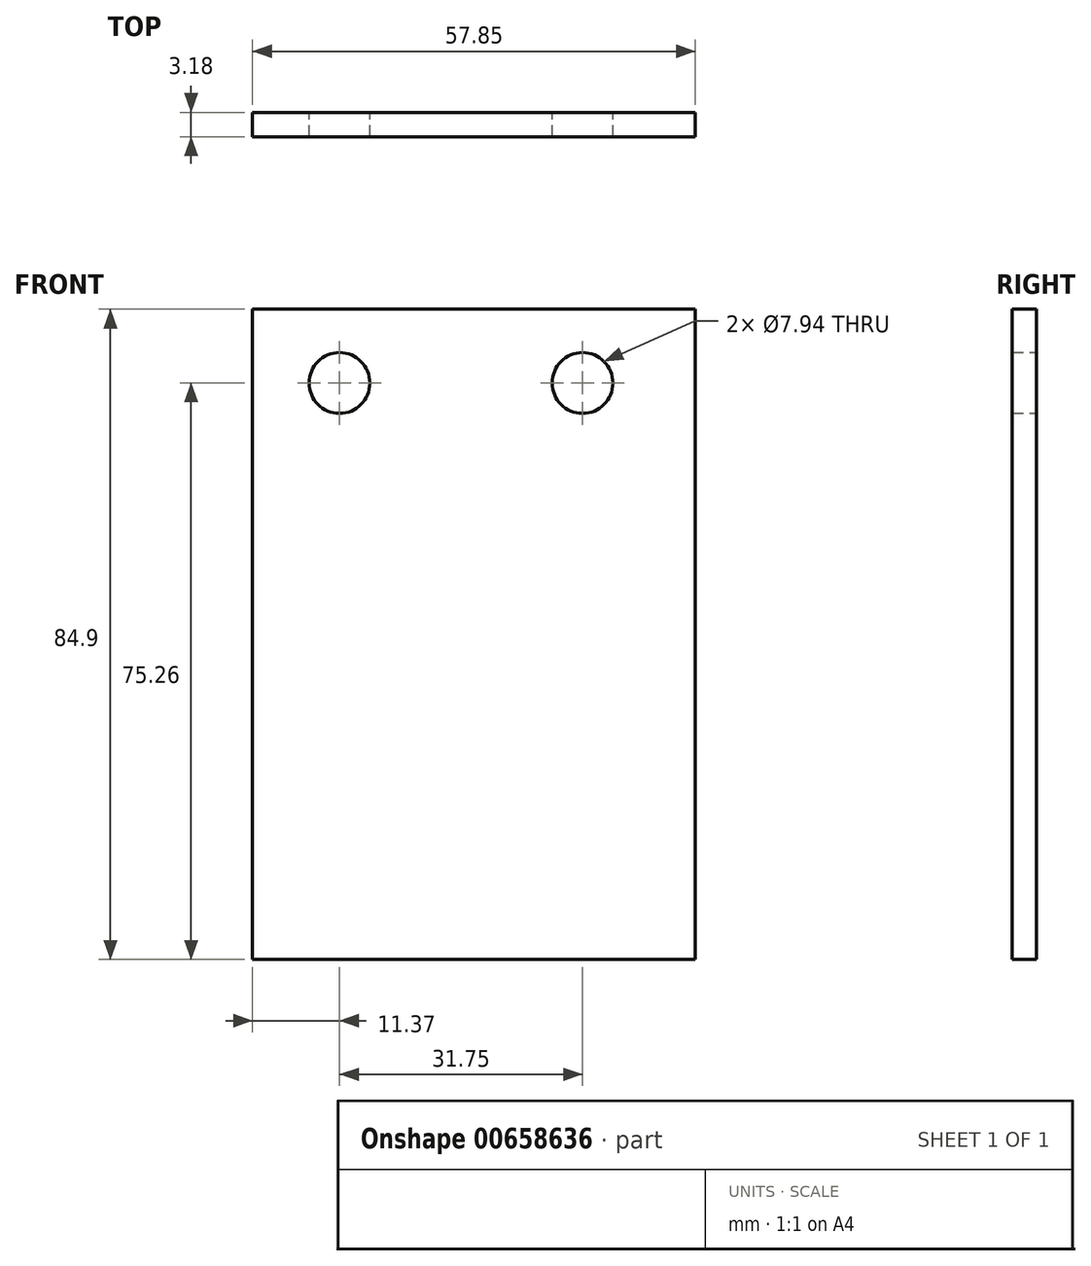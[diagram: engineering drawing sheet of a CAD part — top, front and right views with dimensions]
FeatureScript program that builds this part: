
annotation { "Feature Type Name" : "Feature", "Feature Type Description" : "" }
export const myFeature = defineFeature(function(context is Context, id is Id, definition is map)
    precondition{}
    {
        {
            var Q0;
            Q0=qCreatedBy(makeId("Front.planeOp"),FACE);
            var sketch = newSketch(context, id + "F0", { "sketchPlane" : qUnion([Q0])});
            skCircle(sketch, "E0", {"center": v(0, 0) * mm, "radius": 3.97 * mm});
            skCircle(sketch, "E1", {"center": v(31.75, 0) * mm, "radius": 3.97 * mm});
            skLineSegment(sketch, "E2.bottom", {"start": v(-11.37, 9.64) * mm, "end": v(46.48, 9.64) * mm});
            skLineSegment(sketch, "E2.top", {"start": v(-11.37, -75.26) * mm, "end": v(46.48, -75.26) * mm});
            skLineSegment(sketch, "E2.left", {"start": v(-11.37, 9.64) * mm, "end": v(-11.37, -75.26) * mm});
            skLineSegment(sketch, "E2.right", {"start": v(46.48, 9.64) * mm, "end": v(46.48, -75.26) * mm});
            skSolve(sketch);
        }
        {
            var Q0;
            Q0=makeQuery(id+"F0.imprint","IMPRINT",FACE,{"disambiguationData":[TD([[makeQuery(id+"F0.imprint","IMPRINT",EDGE,{"derivedFrom":sQuery(id+"F0.wireOp",EDGE,"E0")}),-1.0]])]});
            extrude(context, id + "F1", {"entities" : qUnion([Q0]), "depth" : 3.17 * mm, "offsetDistance" : 25.4 * mm});
        }
    });
